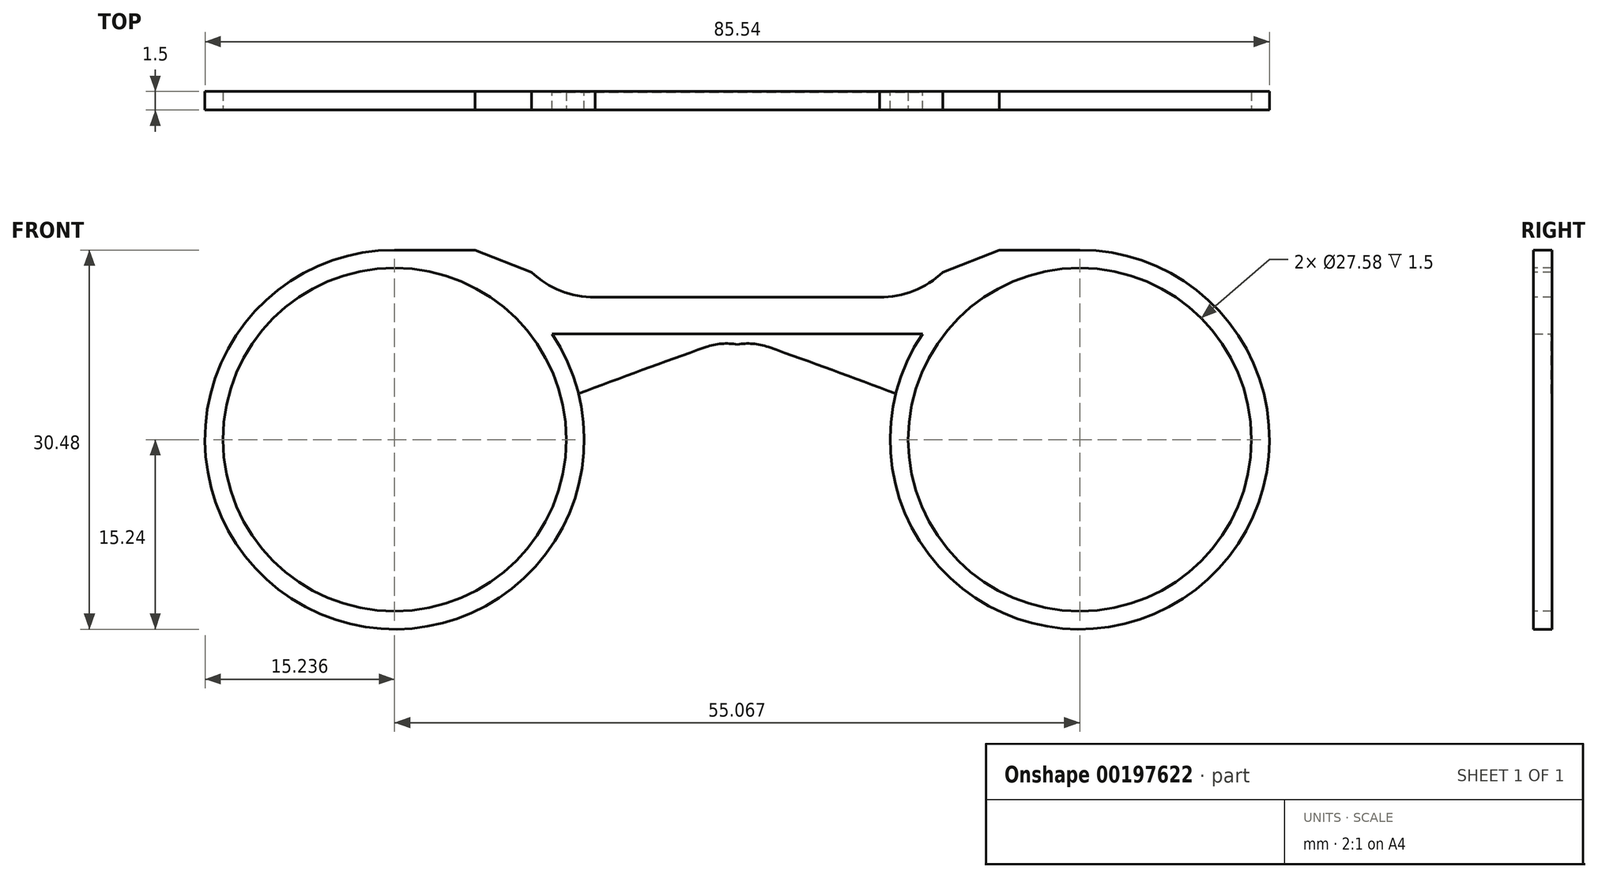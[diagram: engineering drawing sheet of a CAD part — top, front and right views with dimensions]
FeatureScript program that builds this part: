
annotation { "Feature Type Name" : "Feature", "Feature Type Description" : "" }
export const myFeature = defineFeature(function(context is Context, id is Id, definition is map)
    precondition{}
    {
        {
            var Q0;
            Q0=qCreatedBy(makeId("Front.planeOp"),FACE);
            var sketch = newSketch(context, id + "F0", { "sketchPlane" : qUnion([Q0])});
            skCircle(sketch, "E0", {"center": v(-27.53, 0) * mm, "radius": 15.24 * mm});
            skLineSegment(sketch, "E1", {"start": v(0, 11.36) * mm, "end": v(0, -11.47) * mm, "construction": true});
            skPoint(sketch, "E2", {"position": v(-12.3, 0) * mm});
            skCircle(sketch, "E3.MirrorC", {"center": v(27.53, 0) * mm, "radius": 15.24 * mm});
            skPoint(sketch, "E4.MirrorP", {"position": v(12.3, 0) * mm});
            skLineSegment(sketch, "E5", {"start": v(-27.53, 15.24) * mm, "end": v(27.53, 15.24) * mm});
            skLineSegment(sketch, "E6", {"start": v(-14.9, 8.5) * mm, "end": v(14.9, 8.5) * mm});
            skSolve(sketch);
        }
        {
            var Q0;
            Q0 = qSketchRegion(id + "F0", true);
            extrude(context, id + "F1", {"entities" : qUnion([Q0]), "depth" : 1.5 * mm});
        }
        {
            var Q0;
            Q0=makeQuery(id+"F1.opExtrude","CAP_FACE",FACE,{"disambiguationData":[OSD([sQuery(id+"F0.wireOp",EDGE,"E0"),sQuery(id+"F0.wireOp",EDGE,"E3.MirrorC"),sQuery(id+"F0.wireOp",EDGE,"E5"),sQuery(id+"F0.wireOp",EDGE,"E6")])],"isStart":false});
            var sketch = newSketch(context, id + "F2", { "sketchPlane" : qUnion([Q0])});
            skCircle(sketch, "E7", {"center": v(-27.53, 0) * mm, "radius": 13.8 * mm});
            skCircle(sketch, "E8.MirrorC", {"center": v(27.53, 0) * mm, "radius": 13.8 * mm});
            skLineSegment(sketch, "E9", {"start": v(-21.55, 18.48) * mm, "end": v(-16.6, 13.52) * mm});
            skArc(sketch, "E10", {"start": v(-16.6, 13.52) * mm, "mid": v(-14.22, 11.96) * mm, "end": v(-11.43, 11.46) * mm});
            skLineSegment(sketch, "E11", {"start": v(-11.43, 11.46) * mm, "end": v(0, 11.46) * mm});
            skLineSegment(sketch, "E12", {"start": v(0, 11.46) * mm, "end": v(0, 40.36) * mm});
            skLineSegment(sketch, "E13", {"start": v(0, 40.36) * mm, "end": v(-21.55, 18.48) * mm});
            skLineSegment(sketch, "E14", {"start": v(0, -26.36) * mm, "end": v(0, -47.21) * mm});
            skArc(sketch, "E15.MirrorCS", {"start": v(16.6, 13.52) * mm, "mid": v(14.22, 11.96) * mm, "end": v(11.43, 11.46) * mm});
            skLineSegment(sketch, "E16.MirrorCS", {"start": v(21.55, 18.48) * mm, "end": v(16.6, 13.52) * mm});
            skLineSegment(sketch, "E17.MirrorCS", {"start": v(11.43, 11.46) * mm, "end": v(0, 11.46) * mm});
            skLineSegment(sketch, "E18.MirrorCS", {"start": v(0, 40.36) * mm, "end": v(21.55, 18.48) * mm});
            skSolve(sketch);
        }
        {
            var Q0;
            Q0 = qSketchRegion(id + "F2", true);
            extrude(context, id + "F3", {"entities" : qUnion([Q0]), "operationType" : NewBodyOperationType.REMOVE, "oppositeDirection" : true, "depth" : 25.4 * mm});
        }
        {
            var Q0;
            Q0=makeQuery(id+"F1.opExtrude","CAP_FACE",FACE,{"disambiguationData":[OSD([sQuery(id+"F0.wireOp",EDGE,"E0"),sQuery(id+"F0.wireOp",EDGE,"E3.MirrorC"),sQuery(id+"F0.wireOp",EDGE,"E5"),sQuery(id+"F0.wireOp",EDGE,"E6")])],"isStart":false});
            var sketch = newSketch(context, id + "F4", { "sketchPlane" : qUnion([Q0])});
            skLineSegment(sketch, "E19", {"start": v(-24.65, 16.65) * mm, "end": v(-11.43, 11.46) * mm});
            skLineSegment(sketch, "E20", {"start": v(-11.43, 11.46) * mm, "end": v(-9.23, 17.05) * mm});
            skLineSegment(sketch, "E21", {"start": v(-9.23, 17.05) * mm, "end": v(-24.65, 16.65) * mm});
            skLineSegment(sketch, "E22", {"start": v(0, 26.15) * mm, "end": v(0, 39.93) * mm, "construction": true});
            skLineSegment(sketch, "E23.MirrorCS", {"start": v(24.65, 16.65) * mm, "end": v(11.43, 11.46) * mm});
            skLineSegment(sketch, "E24.MirrorCS", {"start": v(11.43, 11.46) * mm, "end": v(9.23, 17.05) * mm});
            skLineSegment(sketch, "E25.MirrorCS", {"start": v(9.23, 17.05) * mm, "end": v(24.65, 16.65) * mm});
            skSolve(sketch);
        }
        {
            var Q0;
            Q0 = qSketchRegion(id + "F4", true);
            extrude(context, id + "F5", {"entities" : qUnion([Q0]), "operationType" : NewBodyOperationType.REMOVE, "oppositeDirection" : true, "depth" : 25.4 * mm});
        }
        {
            assignVariable(context, id + "F6", {"name" : "x", "anyValue" : 0.06});
        }
        {
            var Q0;
            Q0=qCreatedBy(makeId("Front.planeOp"),FACE);
            var sketch = newSketch(context, id + "F7", { "sketchPlane" : qUnion([Q0])});
            skLineSegment(sketch, "E26", {"start": v(0, 61) * mm, "end": v(0, 53.63) * mm, "construction": true});
            skArc(sketch, "E27", {"start": v(-13.42, 3.43) * mm, "mid": v(-15.01, 7.05) * mm, "end": v(-17.61, 10.02) * mm});
            skArc(sketch, "E28", {"start": v(-2.5, 7.44) * mm, "mid": v(-7.98, 5.47) * mm, "end": v(-13.42, 3.43) * mm});
            skArc(sketch, "E29", {"start": v(0, 7.65) * mm, "mid": v(-1.27, 7.7) * mm, "end": v(-2.5, 7.44) * mm});
            skArc(sketch, "E30.MirrorCS", {"start": v(0, 7.65) * mm, "mid": v(1.27, 7.7) * mm, "end": v(2.5, 7.44) * mm});
            skArc(sketch, "E31.MirrorCS", {"start": v(13.42, 3.43) * mm, "mid": v(15.01, 7.05) * mm, "end": v(17.61, 10.02) * mm});
            skArc(sketch, "E32.MirrorCS", {"start": v(2.5, 7.44) * mm, "mid": v(7.98, 5.47) * mm, "end": v(13.42, 3.43) * mm});
            skLineSegment(sketch, "E33", {"start": v(-17.61, 10.02) * mm, "end": v(17.61, 10.02) * mm});
            skSolve(sketch);
        }
        {
            var Q0;
            Q0=makeQuery(id+"F7.imprint","IMPRINT",FACE,{"disambiguationData":[TD([[makeQuery(id+"F7.imprint","IMPRINT",EDGE,{"derivedFrom":sQuery(id+"F7.wireOp",EDGE,"E27")}),-1.0]])]});
            extrude(context, id + "F8", {"entities" : qUnion([Q0]), "operationType" : NewBodyOperationType.ADD, "depth" : (getVariable(context, 'x')) * mm});
        }
    });
